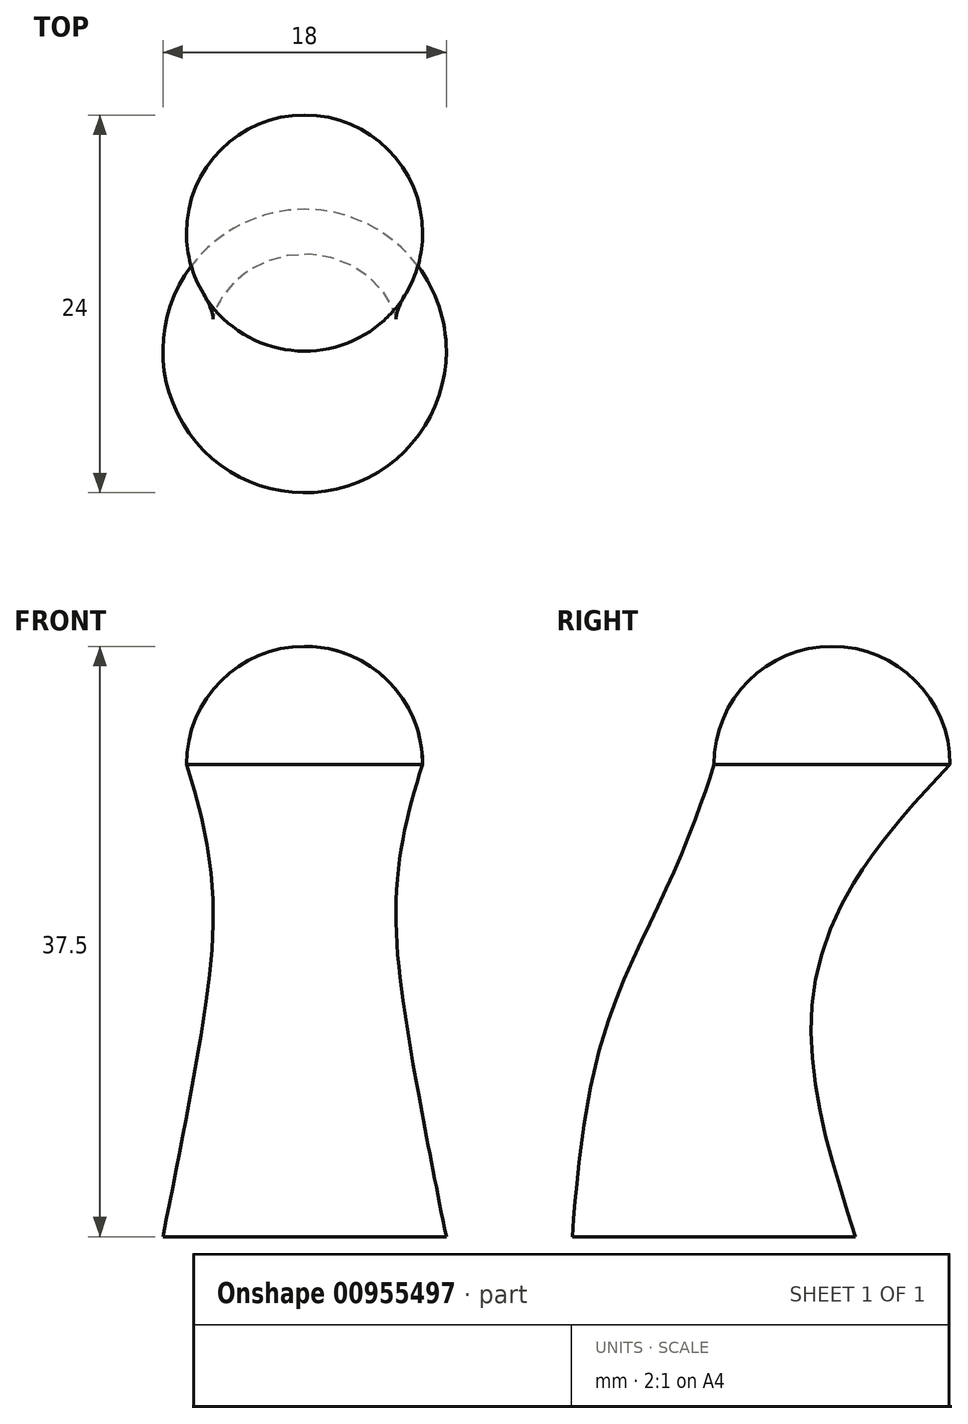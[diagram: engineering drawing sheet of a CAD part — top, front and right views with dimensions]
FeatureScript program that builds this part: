
annotation { "Feature Type Name" : "Feature", "Feature Type Description" : "" }
export const myFeature = defineFeature(function(context is Context, id is Id, definition is map)
    precondition{}
    {
        {
            var Q0;
            Q0=qCreatedBy(makeId("Top.planeOp"),FACE);
            var sketch = newSketch(context, id + "F0", { "sketchPlane" : qUnion([Q0])});
            skCircle(sketch, "E0", {"center": v(0, 0) * mm, "radius": 9 * mm});
            skSolve(sketch);
        }
        {
            var Q0;
            Q0=qCreatedBy(makeId("Top.planeOp"),FACE);
            cPlane(context, id + "F1", {"entities" : qUnion([Q0]), "cplaneType" : CPlaneType.OFFSET, "offset" : 15 * mm, "width" : 150 * mm, "height" : 150 * mm});
        }
        {
            var Q0;
            Q0=qCreatedBy(id+"F1.planeOp",FACE);
            var sketch = newSketch(context, id + "F2", { "sketchPlane" : qUnion([Q0])});
            skCircle(sketch, "E1", {"center": v(0, 0) * mm, "radius": 6.25 * mm});
            skSolve(sketch);
        }
        {
            var Q0;
            Q0=qCreatedBy(id+"F1.planeOp",FACE);
            cPlane(context, id + "F3", {"entities" : qUnion([Q0]), "cplaneType" : CPlaneType.OFFSET, "offset" : 15 * mm, "width" : 150 * mm, "height" : 150 * mm});
        }
        {
            var Q0;
            Q0=qCreatedBy(id+"F3.planeOp",FACE);
            var sketch = newSketch(context, id + "F4", { "sketchPlane" : qUnion([Q0])});
            skCircle(sketch, "E2", {"center": v(0, 7.5) * mm, "radius": 7.5 * mm});
            skSolve(sketch);
        }
        {
            var Q0;
            Q0=sQuery(id+"F0.wireOp",EDGE,"E0");
            var Q1;
            Q1=sQuery(id+"F2.wireOp",EDGE,"E1");
            var Q2;
            Q2=sQuery(id+"F4.wireOp",EDGE,"E2");
            loft(context, id + "F5", {"bodyType" : ToolBodyType.SURFACE, "wireProfilesArray" : [{ "wireProfileEntities" : qUnion([Q0]) }, { "wireProfileEntities" : qUnion([Q1]) }, { "wireProfileEntities" : qUnion([Q2]) }]});
        }
        {
            var Q0;
            Q0=sQuery(id+"F4.wireOp",VERTEX,"E2.center");
            var Q1;
            Q1=qCreatedBy(makeId("Front.planeOp"),FACE);
            cPlane(context, id + "F6", {"entities" : qUnion([Q0, Q1]), "cplaneType" : CPlaneType.PLANE_POINT, "offset" : 25 * mm, "width" : 150 * mm, "height" : 150 * mm});
        }
        {
            var Q0;
            Q0=qCreatedBy(id+"F6.planeOp",FACE);
            var sketch = newSketch(context, id + "F7", { "sketchPlane" : qUnion([Q0])});
            skPoint(sketch, "E3.0", {"position": v(0, 30) * mm});
            skArc(sketch, "E4", {"start": v(-7.5, 30) * mm, "mid": v(-5.3, 35.3) * mm, "end": v(0, 37.5) * mm});
            skLineSegment(sketch, "E5", {"start": v(0, 37.5) * mm, "end": v(0, 30) * mm, "construction": true});
            skSolve(sketch);
        }
        {
            var Q0;
            Q0=sQuery(id+"F7.wireOp",EDGE,"E4");
            var Q1;
            Q1=sQuery(id+"F7.wireOp",EDGE,"E5");
            revolve(context, id + "F8", {"bodyType" : ToolBodyType.SURFACE, "surfaceOperationType" : NewSurfaceOperationType.ADD, "surfaceEntities" : qUnion([Q0]), "axis" : qUnion([Q1]), "revolveType" : RevolveType.FULL});
        }
    });
